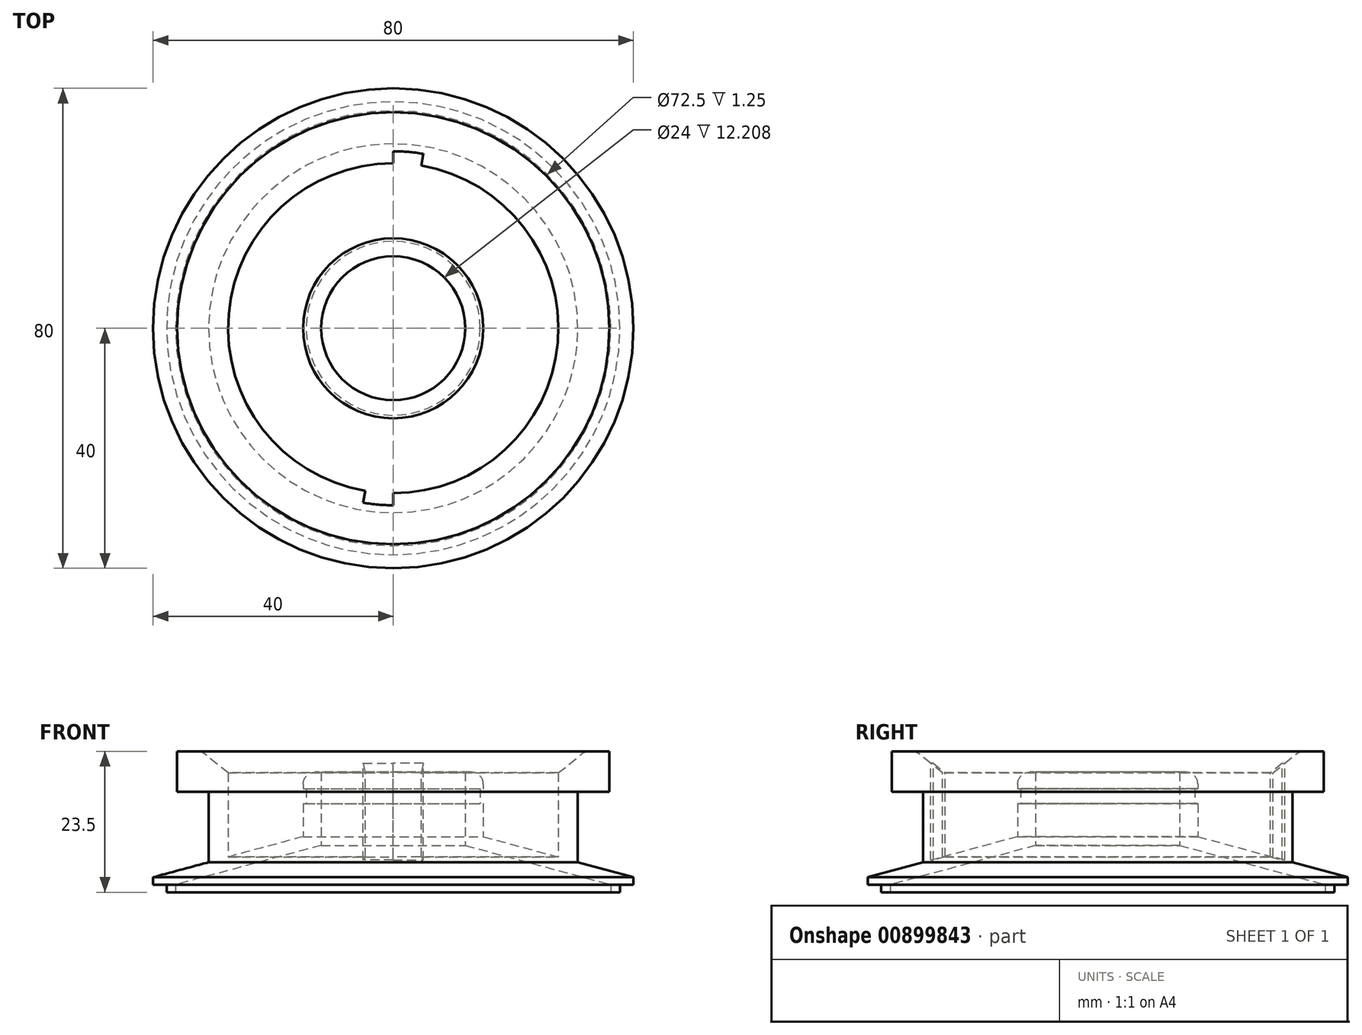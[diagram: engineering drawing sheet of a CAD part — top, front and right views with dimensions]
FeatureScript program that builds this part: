
annotation { "Feature Type Name" : "Feature", "Feature Type Description" : "" }
export const myFeature = defineFeature(function(context is Context, id is Id, definition is map)
    precondition{}
    {
        {
            var Q0;
            Q0=qCreatedBy(makeId("Front.planeOp"),FACE);
            var sketch = newSketch(context, id + "F0", { "sketchPlane" : qUnion([Q0])});
            skLineSegment(sketch, "E0", {"start": v(-40, 0) * mm, "end": v(-40, 1.25) * mm});
            skLineSegment(sketch, "E1", {"start": v(-40, 1.25) * mm, "end": v(-30.75, 3.75) * mm});
            skLineSegment(sketch, "E2", {"start": v(-30.75, 3.75) * mm, "end": v(-30.75, 15.5) * mm});
            skLineSegment(sketch, "E3", {"start": v(-30.75, 15.5) * mm, "end": v(-36, 15.5) * mm});
            skLineSegment(sketch, "E4", {"start": v(-36, 15.5) * mm, "end": v(-36, 22.25) * mm});
            skLineSegment(sketch, "E5", {"start": v(-36, 22.25) * mm, "end": v(-32, 22.25) * mm});
            skLineSegment(sketch, "E6", {"start": v(-32, 22.25) * mm, "end": v(-27.5, 18.63) * mm});
            skLineSegment(sketch, "E7", {"start": v(-27.5, 18.63) * mm, "end": v(-27.5, 4.63) * mm});
            skLineSegment(sketch, "E8", {"start": v(-27.5, 4.63) * mm, "end": v(-15, 8.01) * mm});
            skLineSegment(sketch, "E9", {"start": v(-15, 8.01) * mm, "end": v(-15, 13.51) * mm});
            skLineSegment(sketch, "E10", {"start": v(-15, 13.51) * mm, "end": v(-14.5, 13.51) * mm});
            skLineSegment(sketch, "E11", {"start": v(-14.5, 13.51) * mm, "end": v(-14.5, 16.01) * mm});
            skLineSegment(sketch, "E12", {"start": v(-14.5, 16.01) * mm, "end": v(-15, 16.01) * mm});
            skLineSegment(sketch, "E13", {"start": v(-15, 16.01) * mm, "end": v(-15, 18.76) * mm});
            skLineSegment(sketch, "E14", {"start": v(-15, 18.76) * mm, "end": v(-12, 18.76) * mm});
            skLineSegment(sketch, "E15", {"start": v(-12, 18.76) * mm, "end": v(-12, 6.55) * mm});
            skLineSegment(sketch, "E16", {"start": v(-40, 0) * mm, "end": v(-37.75, 0) * mm});
            skLineSegment(sketch, "E17", {"start": v(-37.75, 0) * mm, "end": v(-37.75, -1.25) * mm});
            skLineSegment(sketch, "E18", {"start": v(-37.75, -1.25) * mm, "end": v(-36.25, -1.25) * mm});
            skLineSegment(sketch, "E19", {"start": v(-36.25, -1.25) * mm, "end": v(-36.25, 0) * mm});
            skLineSegment(sketch, "E20", {"start": v(-36.25, 0) * mm, "end": v(-12, 6.55) * mm});
            skLineSegment(sketch, "E21", {"start": v(0, 0) * mm, "end": v(0, 36.03) * mm, "construction": true});
            skSolve(sketch);
        }
        {
            var Q0;
            Q0=makeQuery(id+"F0.imprint","IMPRINT",FACE,{"disambiguationData":[TD([[makeQuery(id+"F0.imprint","IMPRINT",EDGE,{"derivedFrom":sQuery(id+"F0.wireOp",EDGE,"E0")}),-1.0]])]});
            var Q1;
            Q1=sQuery(id+"F0.wireOp",EDGE,"E21");
            revolve(context, id + "F1", {"surfaceOperationType" : NewSurfaceOperationType.NEW, "entities" : qUnion([Q0]), "axis" : qUnion([Q1]), "revolveType" : RevolveType.FULL});
        }
        {
            var Q0;
            Q0=makeQuery(id+"F1.opRevolve","SWEPT_EDGE",EDGE,{"disambiguationData":[OSD([sQuery(id+"F0.wireOp",EDGE,"E5"),sQuery(id+"F0.wireOp",EDGE,"E6")])]});
            var Q1;
            Q1=makeQuery(id+"F1.opRevolve","SWEPT_EDGE",EDGE,{"disambiguationData":[OSD([sQuery(id+"F0.wireOp",EDGE,"E13"),sQuery(id+"F0.wireOp",EDGE,"E14")])]});
            fillet(context, id + "F2", {"entities" : qUnion([Q0, Q1]), "radius" : 2 * mm, "tangentPropagation" : true, "allowEdgeOverflow" : false});
        }
        {
            var Q0;
            Q0=makeQuery(id+"F1.opRevolve","SWEPT_FACE",FACE,{"disambiguationData":[OSD([sQuery(id+"F0.wireOp",EDGE,"E5")])]});
            var sketch = newSketch(context, id + "F3", { "sketchPlane" : qUnion([Q0])});
            skArc(sketch, "E22", {"start": v(0, 29.5) * mm, "mid": v(2.5, 29.4) * mm, "end": v(5, 29.07) * mm});
            skArc(sketch, "E23", {"start": v(0, 27.5) * mm, "mid": v(2.34, 27.4) * mm, "end": v(4.66, 27.1) * mm});
            skLineSegment(sketch, "E24", {"start": v(0, 27.5) * mm, "end": v(0, 29.5) * mm});
            skLineSegment(sketch, "E25", {"start": v(5, 29.07) * mm, "end": v(4.66, 27.1) * mm});
            skLineSegment(sketch, "E26.MirrorCS", {"start": v(0, -27.5) * mm, "end": v(0, -29.5) * mm});
            skArc(sketch, "E27.MirrorCS", {"start": v(0, -29.5) * mm, "mid": v(-2.5, -29.4) * mm, "end": v(-5, -29.07) * mm});
            skArc(sketch, "E28.MirrorCS", {"start": v(0, -27.5) * mm, "mid": v(-2.34, -27.4) * mm, "end": v(-4.66, -27.1) * mm});
            skLineSegment(sketch, "E29.MirrorCS", {"start": v(-5, -29.07) * mm, "end": v(-4.66, -27.1) * mm});
            skSolve(sketch);
        }
        {
            var Q0;
            Q0 = qSketchRegion(id + "F3", true);
            var Q1;
            Q1=makeQuery(id+"F1.opRevolve","SWEPT_FACE",FACE,{"disambiguationData":[OSD([sQuery(id+"F0.wireOp",EDGE,"E8")])]});
            extrude(context, id + "F4", {"entities" : qUnion([Q0]), "operationType" : NewBodyOperationType.REMOVE, "endBound" : BoundingType.UP_TO_SURFACE, "oppositeDirection" : true, "depth" : 0 * mm, "endBoundEntityFace" : qUnion([Q1]), "offsetDistance" : 25 * mm});
        }
    });
